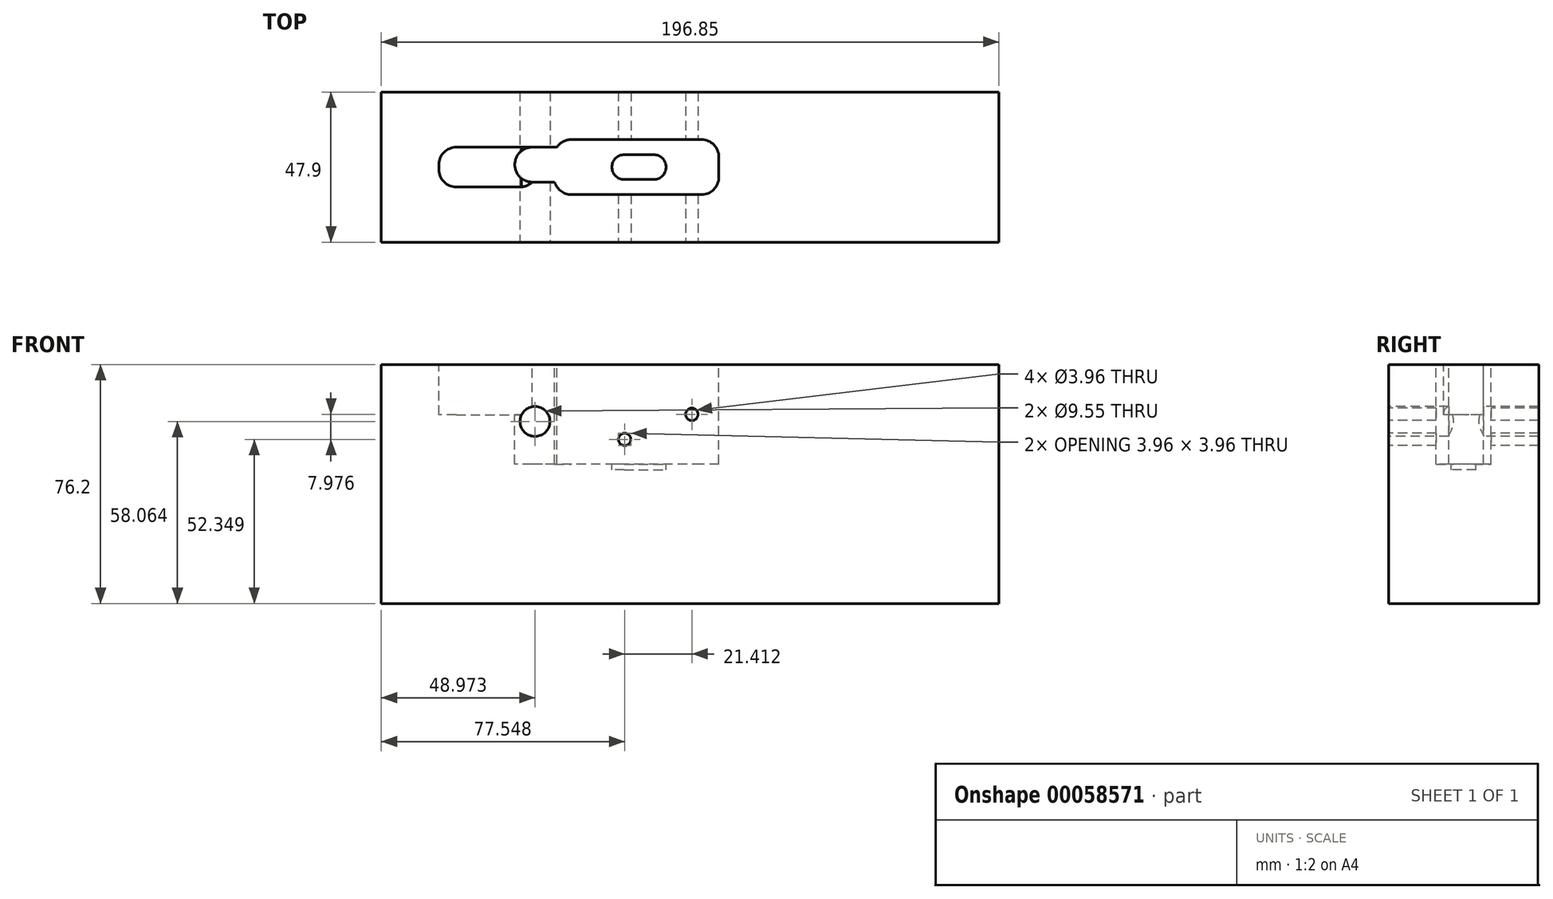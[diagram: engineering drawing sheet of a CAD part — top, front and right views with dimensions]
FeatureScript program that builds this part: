
annotation { "Feature Type Name" : "Feature", "Feature Type Description" : "" }
export const myFeature = defineFeature(function(context is Context, id is Id, definition is map)
    precondition{}
    {
        {
            var Q0;
            Q0=qCreatedBy(makeId("Top.planeOp"),FACE);
            var sketch = newSketch(context, id + "F0", { "sketchPlane" : qUnion([Q0])});
            skLineSegment(sketch, "E0.bottom", {"start": v(-98.96, 23.95) * mm, "end": v(97.9, 23.95) * mm});
            skLineSegment(sketch, "E0.top", {"start": v(-98.96, -23.95) * mm, "end": v(97.9, -23.95) * mm});
            skLineSegment(sketch, "E0.left", {"start": v(-98.96, 23.95) * mm, "end": v(-98.96, -23.95) * mm});
            skLineSegment(sketch, "E0.right", {"start": v(97.9, 23.95) * mm, "end": v(97.9, -23.95) * mm});
            skSolve(sketch);
        }
        {
            var Q0;
            Q0=makeQuery(id+"F0.imprint","IMPRINT",FACE,{"disambiguationData":[TD([[makeQuery(id+"F0.imprint","IMPRINT",EDGE,{"derivedFrom":sQuery(id+"F0.wireOp",EDGE,"E0.bottom")}),-1.0]])]});
            extrude(context, id + "F1", {"entities" : qUnion([Q0]), "oppositeDirection" : true, "depth" : 76.2 * mm});
        }
        {
            var Q0;
            Q0=makeQuery(id+"F1.opExtrude","SWEPT_FACE",FACE,{"disambiguationData":[OSD([sQuery(id+"F0.wireOp",EDGE,"E0.top")])]});
            var sketch = newSketch(context, id + "F2", { "sketchPlane" : qUnion([Q0])});
            skCircle(sketch, "E1", {"center": v(91.54, -6.35) * mm, "radius": 3.18 * mm, "construction": true});
            skCircle(sketch, "E2", {"center": v(-70.38, -6.35) * mm, "radius": 3.18 * mm, "construction": true});
            skCircle(sketch, "E3", {"center": v(-49.99, -18.14) * mm, "radius": 4.78 * mm});
            skCircle(sketch, "E4", {"center": v(-21.41, -23.85) * mm, "radius": 1.98 * mm});
            skCircle(sketch, "E5", {"center": v(0, -15.87) * mm, "radius": 1.98 * mm});
            skSolve(sketch);
        }
        {
            var Q0;
            Q0=qSketchRegion(id+"F2",true);
            extrude(context, id + "F3", {"entities" : qUnion([Q0]), "operationType" : NewBodyOperationType.REMOVE, "endBound" : BoundingType.THROUGH_ALL, "oppositeDirection" : true, "depth" : 25.4 * mm});
        }
        {
            var Q0;
            Q0=makeQuery(id+"F0.imprint","IMPRINT",FACE,{"disambiguationData":[TD([[makeQuery(id+"F0.imprint","IMPRINT",EDGE,{"derivedFrom":sQuery(id+"F0.wireOp",EDGE,"E0.bottom")}),-1.0]])]});
            var sketch = newSketch(context, id + "F4", { "sketchPlane" : qUnion([Q0])});
            skLineSegment(sketch, "E6.bottom", {"start": v(3.07, 8.76) * mm, "end": v(-38.4, 8.76) * mm});
            skLineSegment(sketch, "E6.top", {"start": v(3.07, -8.76) * mm, "end": v(-38.4, -8.76) * mm});
            skLineSegment(sketch, "E6.left", {"start": v(8.61, 3.23) * mm, "end": v(8.61, -3.23) * mm});
            skPoint(sketch, "E7.visualSharp", {"position": v(-43.94, 8.76) * mm});
            skArc(sketch, "E7.filletArc", {"start": v(-38.4, 8.76) * mm, "mid": v(-40.99, 8.12) * mm, "end": v(-42.98, 6.35) * mm});
            skPoint(sketch, "E8.visualSharp", {"position": v(8.61, 8.76) * mm});
            skArc(sketch, "E8.filletArc", {"start": v(8.61, 3.23) * mm, "mid": v(6.99, 7.14) * mm, "end": v(3.07, 8.76) * mm});
            skPoint(sketch, "E9.visualSharp", {"position": v(-43.94, -8.76) * mm});
            skArc(sketch, "E9.filletArc", {"start": v(-43.72, -4.78) * mm, "mid": v(-41.73, -7.66) * mm, "end": v(-38.4, -8.76) * mm});
            skPoint(sketch, "E10.visualSharp", {"position": v(8.61, -8.76) * mm});
            skArc(sketch, "E10.filletArc", {"start": v(3.07, -8.76) * mm, "mid": v(6.99, -7.14) * mm, "end": v(8.61, -3.23) * mm});
            skLineSegment(sketch, "E11.bottom", {"start": v(-42.98, 6.35) * mm, "end": v(-50.88, 6.35) * mm});
            skLineSegment(sketch, "E11.top", {"start": v(-43.72, -4.78) * mm, "end": v(-50.88, -4.78) * mm});
            skLineSegment(sketch, "E11.right", {"start": v(-56.41, 6.35) * mm, "end": v(-56.41, -4.78) * mm});
            skLineSegment(sketch, "E12", {"start": v(-56.41, 6.35) * mm, "end": v(-56.41, 6.35) * mm});
            skLineSegment(sketch, "E13", {"start": v(-56.41, 0.81) * mm, "end": v(-56.41, 0.76) * mm});
            skPoint(sketch, "E14.visualSharp", {"position": v(-56.41, 6.35) * mm});
            skArc(sketch, "E14.filletArc", {"start": v(-50.88, 6.35) * mm, "mid": v(-52.7, 6.04) * mm, "end": v(-54.32, 5.14) * mm});
            skPoint(sketch, "E15.visualSharp", {"position": v(-56.41, 0.81) * mm});
            skArc(sketch, "E15.filletArc", {"start": v(-54.32, 5.14) * mm, "mid": v(-55.86, 3.22) * mm, "end": v(-56.41, 0.81) * mm});
            skPoint(sketch, "E16.visualSharp", {"position": v(-56.41, -4.78) * mm});
            skArc(sketch, "E16.filletArc", {"start": v(-56.41, 0.76) * mm, "mid": v(-54.8, -3.15) * mm, "end": v(-50.88, -4.78) * mm});
            skSolve(sketch);
        }
        {
            var Q0;
            Q0=qSketchRegion(id+"F4",true);
            extrude(context, id + "F5", {"entities" : qUnion([Q0]), "operationType" : NewBodyOperationType.REMOVE, "oppositeDirection" : true, "depth" : 31.72 * mm});
        }
        {
            var Q0;
            Q0=makeQuery(id+"F0.imprint","IMPRINT",FACE,{"disambiguationData":[TD([[makeQuery(id+"F0.imprint","IMPRINT",EDGE,{"derivedFrom":sQuery(id+"F0.wireOp",EDGE,"E0.bottom")}),-1.0]])]});
            var sketch = newSketch(context, id + "F6", { "sketchPlane" : qUnion([Q0])});
            skLineSegment(sketch, "E17.bottom", {"start": v(-75.06, 6.35) * mm, "end": v(-49.23, 6.35) * mm});
            skLineSegment(sketch, "E17.top", {"start": v(-75.06, -6.35) * mm, "end": v(-54.76, -6.35) * mm});
            skLineSegment(sketch, "E17.left", {"start": v(-80.6, 0.81) * mm, "end": v(-80.6, -0.81) * mm});
            skPoint(sketch, "E18.visualSharp", {"position": v(-80.6, 6.35) * mm});
            skArc(sketch, "E18.filletArc", {"start": v(-75.06, 6.35) * mm, "mid": v(-78.97, 4.73) * mm, "end": v(-80.6, 0.81) * mm});
            skPoint(sketch, "E19.visualSharp", {"position": v(-80.6, -6.35) * mm});
            skArc(sketch, "E19.filletArc", {"start": v(-80.6, -0.81) * mm, "mid": v(-78.97, -4.73) * mm, "end": v(-75.06, -6.35) * mm});
            skArc(sketch, "E20.filletArc", {"start": v(-54.76, -6.35) * mm, "mid": v(-50.85, -4.73) * mm, "end": v(-49.23, -0.81) * mm});
            skLineSegment(sketch, "E21", {"start": v(-49.23, 6.35) * mm, "end": v(-49.23, -0.81) * mm});
            skSolve(sketch);
        }
        {
            var Q0;
            Q0=qSketchRegion(id+"F6",true);
            extrude(context, id + "F7", {"entities" : qUnion([Q0]), "operationType" : NewBodyOperationType.REMOVE, "oppositeDirection" : true, "depth" : 16 * mm});
        }
        {
            var Q0;
            Q0=makeQuery(id+"F0.imprint","IMPRINT",FACE,{"disambiguationData":[TD([[makeQuery(id+"F0.imprint","IMPRINT",EDGE,{"derivedFrom":sQuery(id+"F0.wireOp",EDGE,"E0.bottom")}),-1.0]])]});
            var sketch = newSketch(context, id + "F8", { "sketchPlane" : qUnion([Q0])});
            skLineSegment(sketch, "E22.bottom", {"start": v(-21.51, 3.96) * mm, "end": v(-12.17, 3.96) * mm});
            skLineSegment(sketch, "E22.top", {"start": v(-21.51, -3.96) * mm, "end": v(-12.17, -3.96) * mm});
            skLineSegment(sketch, "E22.left", {"start": v(-25.48, 0) * mm, "end": v(-25.48, 0) * mm});
            skLineSegment(sketch, "E22.right", {"start": v(-8.2, 0) * mm, "end": v(-8.2, 0) * mm});
            skPoint(sketch, "E23.visualSharp", {"position": v(-25.48, 3.96) * mm});
            skArc(sketch, "E23.filletArc", {"start": v(-21.51, 3.96) * mm, "mid": v(-24.32, 2.8) * mm, "end": v(-25.48, 0) * mm});
            skPoint(sketch, "E24.visualSharp", {"position": v(-25.48, -3.96) * mm});
            skArc(sketch, "E24.filletArc", {"start": v(-25.48, 0) * mm, "mid": v(-24.32, -2.8) * mm, "end": v(-21.51, -3.96) * mm});
            skPoint(sketch, "E25.visualSharp", {"position": v(-8.2, -3.96) * mm});
            skArc(sketch, "E25.filletArc", {"start": v(-12.17, -3.96) * mm, "mid": v(-9.36, -2.8) * mm, "end": v(-8.2, 0) * mm});
            skPoint(sketch, "E26.visualSharp", {"position": v(-8.2, 3.96) * mm});
            skArc(sketch, "E26.filletArc", {"start": v(-8.2, 0) * mm, "mid": v(-9.36, 2.8) * mm, "end": v(-12.17, 3.96) * mm});
            skSolve(sketch);
        }
        {
            var Q0;
            Q0=qSketchRegion(id+"F8",true);
            extrude(context, id + "F9", {"entities" : qUnion([Q0]), "operationType" : NewBodyOperationType.REMOVE, "oppositeDirection" : true, "offsetDistance" : 25.4 * mm, "depth" : 33.53 * mm});
        }
    });
